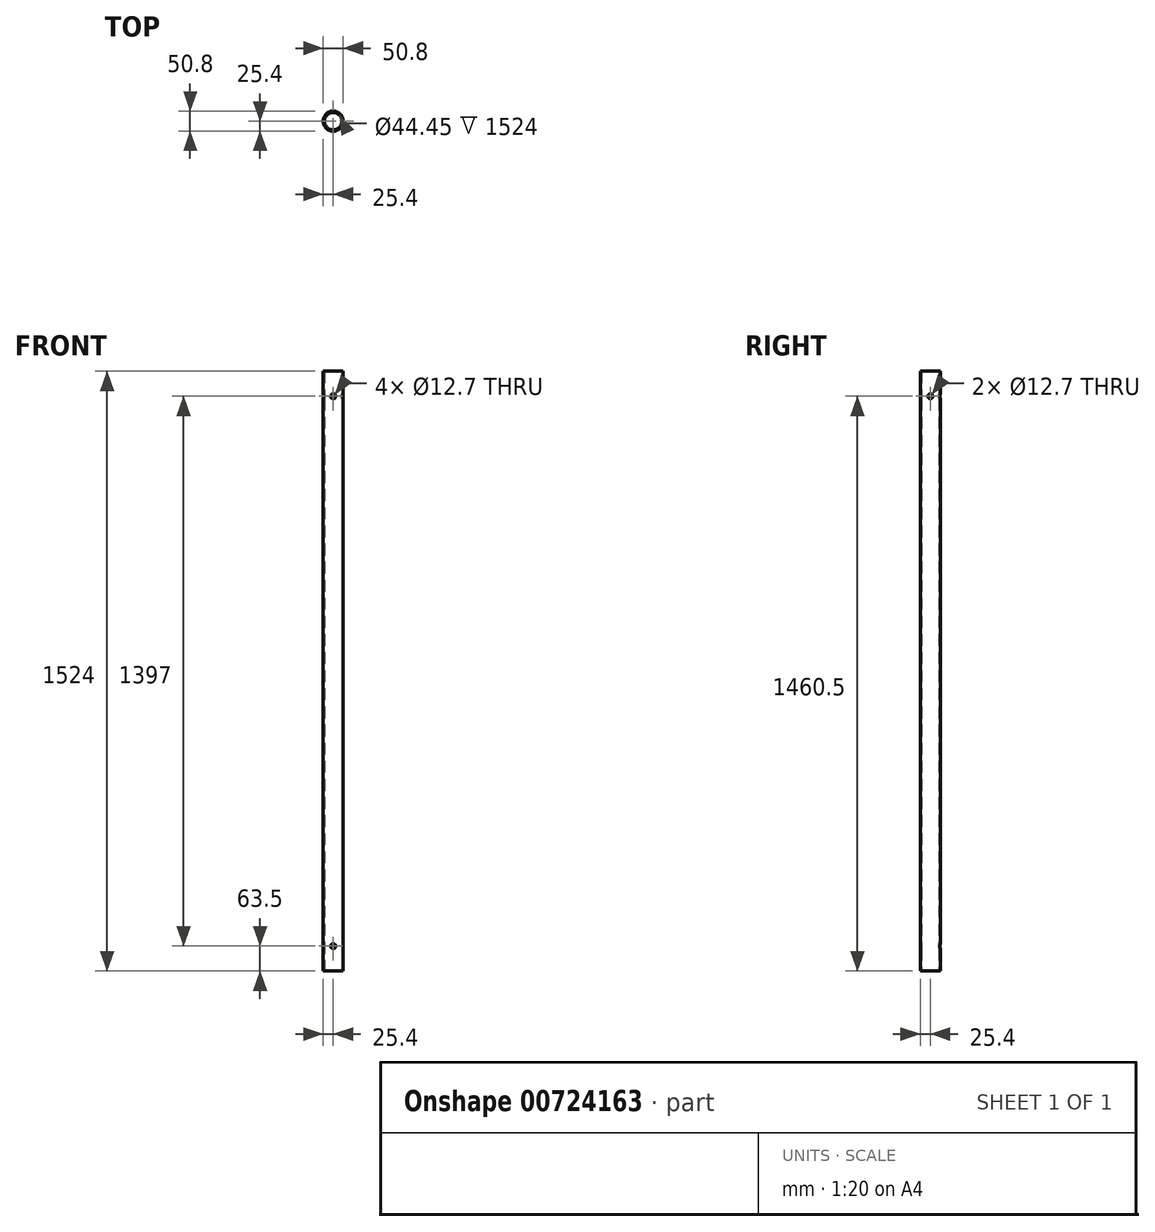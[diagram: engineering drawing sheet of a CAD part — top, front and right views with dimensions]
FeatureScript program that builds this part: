
annotation { "Feature Type Name" : "Feature", "Feature Type Description" : "" }
export const myFeature = defineFeature(function(context is Context, id is Id, definition is map)
    precondition{}
    {
        {
            var Q0;
            Q0=qCreatedBy(makeId("Top.planeOp"),FACE);
            var sketch = newSketch(context, id + "F0", { "sketchPlane" : qUnion([Q0])});
            skCircle(sketch, "E0", {"center": v(0, 0) * mm, "radius": 25.4 * mm});
            skCircle(sketch, "E1", {"center": v(0, 0) * mm, "radius": 22.23 * mm});
            skSolve(sketch);
        }
        {
            var Q0;
            Q0=makeQuery(id+"F0.imprint","IMPRINT",FACE,{"disambiguationData":[TD([[makeQuery(id+"F0.imprint","IMPRINT",EDGE,{"derivedFrom":sQuery(id+"F0.wireOp",EDGE,"E0")}),1.0]])]});
            extrude(context, id + "F1", {"entities" : qUnion([Q0]), "depth" : 1524 * mm, "offsetDistance" : 25.4 * mm});
        }
        {
            var Q0;
            Q0=qCreatedBy(makeId("Front.planeOp"),FACE);
            var sketch = newSketch(context, id + "F2", { "sketchPlane" : qUnion([Q0])});
            skLineSegment(sketch, "E2", {"start": v(0, 0) * mm, "end": v(0, 63.5) * mm, "construction": true});
            skLineSegment(sketch, "E3", {"start": v(0, 63.5) * mm, "end": v(0, 1460.5) * mm, "construction": true});
            skCircle(sketch, "E4", {"center": v(0, 1460.5) * mm, "radius": 6.35 * mm});
            skCircle(sketch, "E5", {"center": v(0, 63.5) * mm, "radius": 6.35 * mm});
            skSolve(sketch);
        }
        {
            var Q0;
            Q0=qSketchRegion(id+"F2",true);
            extrude(context, id + "F3", {"entities" : qUnion([Q0]), "operationType" : NewBodyOperationType.REMOVE, "oppositeDirection" : true, "depth" : 50.8 * mm, "offsetDistance" : 25.4 * mm, "symmetric" : true});
        }
        {
            var Q0;
            Q0=qCreatedBy(makeId("Right.planeOp"),FACE);
            var sketch = newSketch(context, id + "F4", { "sketchPlane" : qUnion([Q0])});
            skCircle(sketch, "E6", {"center": v(0, 1460.5) * mm, "radius": 6.35 * mm});
            skSolve(sketch);
        }
        {
            var Q0;
            Q0 = qSketchRegion(id + "F4", true);
            extrude(context, id + "F5", {"entities" : qUnion([Q0]), "operationType" : NewBodyOperationType.REMOVE, "oppositeDirection" : true, "depth" : 76.2 * mm, "offsetDistance" : 25.4 * mm, "symmetric" : true});
        }
    });
